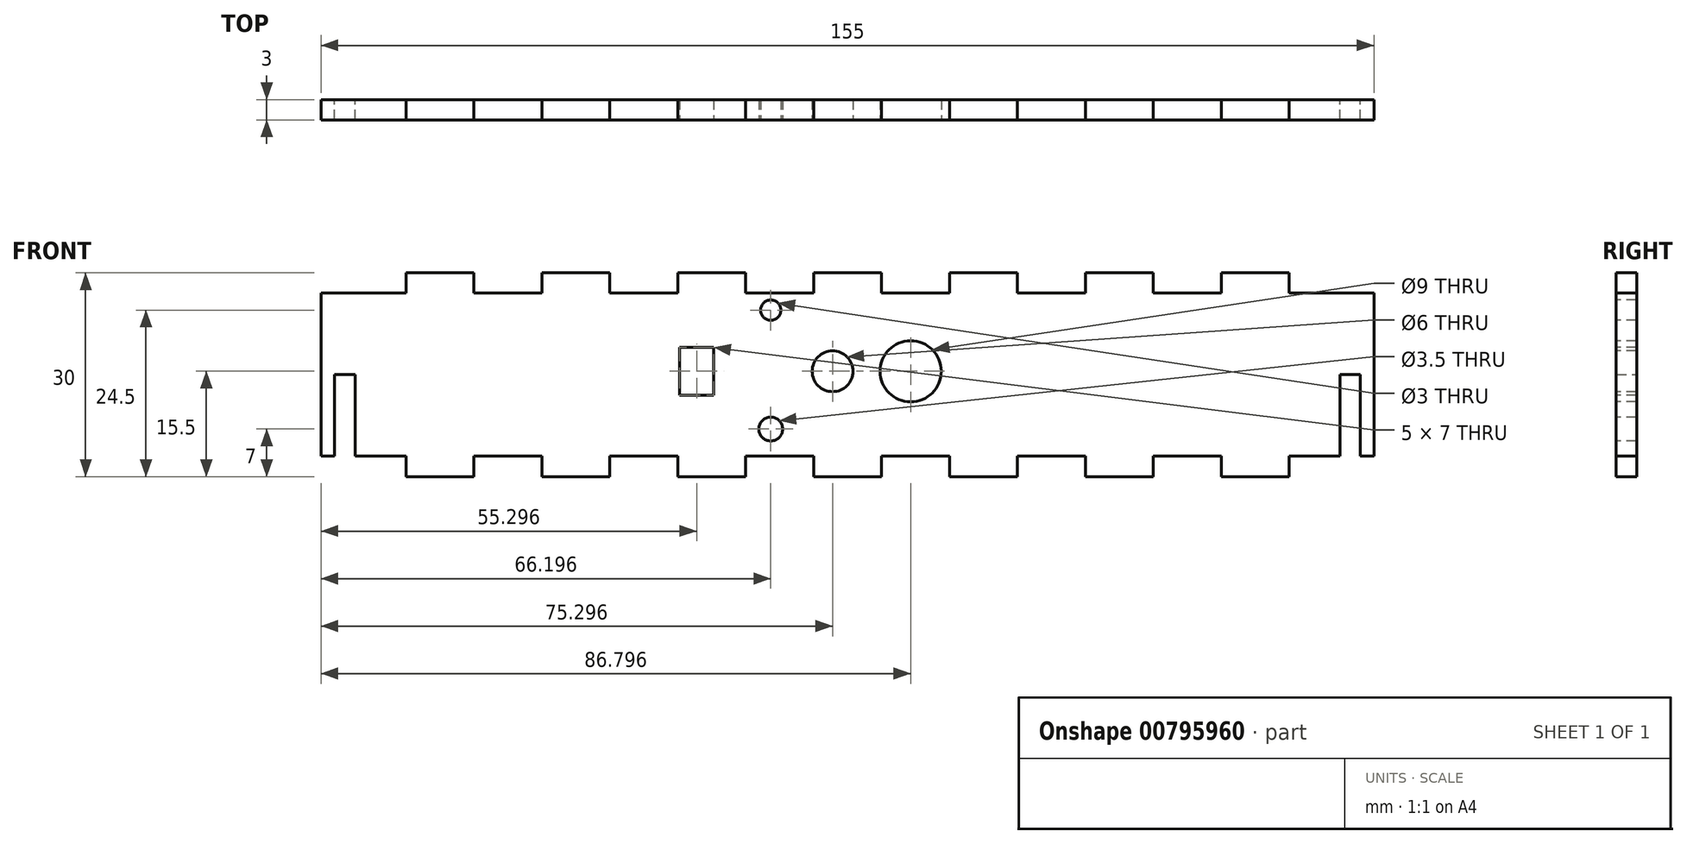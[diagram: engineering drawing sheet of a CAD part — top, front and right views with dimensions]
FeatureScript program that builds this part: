
annotation { "Feature Type Name" : "Feature", "Feature Type Description" : "" }
export const myFeature = defineFeature(function(context is Context, id is Id, definition is map)
    precondition{}
    {
        {
            var Q0;
            Q0=qCreatedBy(makeId("Front.planeOp"),FACE);
            var sketch = newSketch(context, id + "F0", { "sketchPlane" : qUnion([Q0])});
            skLineSegment(sketch, "E0.bottom", {"start": v(75.5, 15) * mm, "end": v(-75.5, 15) * mm});
            skLineSegment(sketch, "E0.top", {"start": v(75.5, -15) * mm, "end": v(-75.5, -15) * mm});
            skLineSegment(sketch, "E0.left", {"start": v(75.5, 15) * mm, "end": v(75.5, -15) * mm});
            skLineSegment(sketch, "E0.right", {"start": v(-75.5, 15) * mm, "end": v(-75.5, -15) * mm});
            skPoint(sketch, "E0.middle", {"position": v(0, 0) * mm});
            skSolve(sketch);
        }
        {
            var Q0;
            Q0=makeQuery(id+"F0.imprint","IMPRINT",FACE,{"disambiguationData":[TD([[makeQuery(id+"F0.imprint","IMPRINT",EDGE,{"derivedFrom":sQuery(id+"F0.wireOp",EDGE,"E0.bottom")}),1.0]])]});
            extrude(context, id + "F1", {"entities" : qUnion([Q0]), "depth" : 3 * mm, "offsetDistance" : 25 * mm});
        }
        {
            var Q0;
            Q0=makeQuery(id+"F1.opExtrude","CAP_FACE",FACE,{"disambiguationData":[OSD([sQuery(id+"F0.wireOp",EDGE,"E0.bottom"),sQuery(id+"F0.wireOp",EDGE,"E0.top"),sQuery(id+"F0.wireOp",EDGE,"E0.left"),sQuery(id+"F0.wireOp",EDGE,"E0.right")])],"isStart":false});
            var sketch = newSketch(context, id + "F2", { "sketchPlane" : qUnion([Q0])});
            skLineSegment(sketch, "E1.bottom", {"start": v(-75, -15) * mm, "end": v(-65, -15) * mm});
            skLineSegment(sketch, "E1.top", {"start": v(-75, -12) * mm, "end": v(-65, -12) * mm});
            skLineSegment(sketch, "E1.left", {"start": v(-75, -15) * mm, "end": v(-75, -12) * mm});
            skLineSegment(sketch, "E1.right", {"start": v(-65, -15) * mm, "end": v(-65, -12) * mm});
            skLineSegment(sketch, "E2.0.1.0", {"start": v(-75, 12) * mm, "end": v(-65, 12) * mm});
            skLineSegment(sketch, "E2.0.1.1", {"start": v(-75, 15) * mm, "end": v(-65, 15) * mm});
            skLineSegment(sketch, "E2.0.1.2", {"start": v(-75, 12) * mm, "end": v(-75, 15) * mm});
            skLineSegment(sketch, "E2.0.1.3", {"start": v(-65, 12) * mm, "end": v(-65, 15) * mm});
            skLineSegment(sketch, "E2.1.0.0", {"start": v(-55, -15) * mm, "end": v(-45, -15) * mm});
            skLineSegment(sketch, "E2.1.0.1", {"start": v(-55, -12) * mm, "end": v(-45, -12) * mm});
            skLineSegment(sketch, "E2.1.0.2", {"start": v(-55, -15) * mm, "end": v(-55, -12) * mm});
            skLineSegment(sketch, "E2.1.0.3", {"start": v(-45, -15) * mm, "end": v(-45, -12) * mm});
            skLineSegment(sketch, "E2.1.1.0", {"start": v(-55, 12) * mm, "end": v(-45, 12) * mm});
            skLineSegment(sketch, "E2.1.1.1", {"start": v(-55, 15) * mm, "end": v(-45, 15) * mm});
            skLineSegment(sketch, "E2.1.1.2", {"start": v(-55, 12) * mm, "end": v(-55, 15) * mm});
            skLineSegment(sketch, "E2.1.1.3", {"start": v(-45, 12) * mm, "end": v(-45, 15) * mm});
            skLineSegment(sketch, "E2.2.0.0", {"start": v(-35, -15) * mm, "end": v(-25, -15) * mm});
            skLineSegment(sketch, "E2.2.0.1", {"start": v(-35, -12) * mm, "end": v(-25, -12) * mm});
            skLineSegment(sketch, "E2.2.0.2", {"start": v(-35, -15) * mm, "end": v(-35, -12) * mm});
            skLineSegment(sketch, "E2.2.0.3", {"start": v(-25, -15) * mm, "end": v(-25, -12) * mm});
            skLineSegment(sketch, "E2.2.1.0", {"start": v(-35, 12) * mm, "end": v(-25, 12) * mm});
            skLineSegment(sketch, "E2.2.1.1", {"start": v(-35, 15) * mm, "end": v(-25, 15) * mm});
            skLineSegment(sketch, "E2.2.1.2", {"start": v(-35, 12) * mm, "end": v(-35, 15) * mm});
            skLineSegment(sketch, "E2.2.1.3", {"start": v(-25, 12) * mm, "end": v(-25, 15) * mm});
            skLineSegment(sketch, "E2.3.0.0", {"start": v(-15, -15) * mm, "end": v(-5, -15) * mm});
            skLineSegment(sketch, "E2.3.0.1", {"start": v(-15, -12) * mm, "end": v(-5, -12) * mm});
            skLineSegment(sketch, "E2.3.0.2", {"start": v(-15, -15) * mm, "end": v(-15, -12) * mm});
            skLineSegment(sketch, "E2.3.0.3", {"start": v(-5, -15) * mm, "end": v(-5, -12) * mm});
            skLineSegment(sketch, "E2.3.1.0", {"start": v(-15, 12) * mm, "end": v(-5, 12) * mm});
            skLineSegment(sketch, "E2.3.1.1", {"start": v(-15, 15) * mm, "end": v(-5, 15) * mm});
            skLineSegment(sketch, "E2.3.1.2", {"start": v(-15, 12) * mm, "end": v(-15, 15) * mm});
            skLineSegment(sketch, "E2.3.1.3", {"start": v(-5, 12) * mm, "end": v(-5, 15) * mm});
            skLineSegment(sketch, "E2.4.0.0", {"start": v(5, -15) * mm, "end": v(15, -15) * mm});
            skLineSegment(sketch, "E2.4.0.1", {"start": v(5, -12) * mm, "end": v(15, -12) * mm});
            skLineSegment(sketch, "E2.4.0.2", {"start": v(5, -15) * mm, "end": v(5, -12) * mm});
            skLineSegment(sketch, "E2.4.0.3", {"start": v(15, -15) * mm, "end": v(15, -12) * mm});
            skLineSegment(sketch, "E2.4.1.0", {"start": v(5, 12) * mm, "end": v(15, 12) * mm});
            skLineSegment(sketch, "E2.4.1.1", {"start": v(5, 15) * mm, "end": v(15, 15) * mm});
            skLineSegment(sketch, "E2.4.1.2", {"start": v(5, 12) * mm, "end": v(5, 15) * mm});
            skLineSegment(sketch, "E2.4.1.3", {"start": v(15, 12) * mm, "end": v(15, 15) * mm});
            skLineSegment(sketch, "E2.5.0.0", {"start": v(25, -15) * mm, "end": v(35, -15) * mm});
            skLineSegment(sketch, "E2.5.0.1", {"start": v(25, -12) * mm, "end": v(35, -12) * mm});
            skLineSegment(sketch, "E2.5.0.2", {"start": v(25, -15) * mm, "end": v(25, -12) * mm});
            skLineSegment(sketch, "E2.5.0.3", {"start": v(35, -15) * mm, "end": v(35, -12) * mm});
            skLineSegment(sketch, "E2.5.1.0", {"start": v(25, 12) * mm, "end": v(35, 12) * mm});
            skLineSegment(sketch, "E2.5.1.1", {"start": v(25, 15) * mm, "end": v(35, 15) * mm});
            skLineSegment(sketch, "E2.5.1.2", {"start": v(25, 12) * mm, "end": v(25, 15) * mm});
            skLineSegment(sketch, "E2.5.1.3", {"start": v(35, 12) * mm, "end": v(35, 15) * mm});
            skLineSegment(sketch, "E2.6.0.0", {"start": v(45, -15) * mm, "end": v(55, -15) * mm});
            skLineSegment(sketch, "E2.6.0.1", {"start": v(45, -12) * mm, "end": v(55, -12) * mm});
            skLineSegment(sketch, "E2.6.0.2", {"start": v(45, -15) * mm, "end": v(45, -12) * mm});
            skLineSegment(sketch, "E2.6.0.3", {"start": v(55, -15) * mm, "end": v(55, -12) * mm});
            skLineSegment(sketch, "E2.6.1.0", {"start": v(45, 12) * mm, "end": v(55, 12) * mm});
            skLineSegment(sketch, "E2.6.1.1", {"start": v(45, 15) * mm, "end": v(55, 15) * mm});
            skLineSegment(sketch, "E2.6.1.2", {"start": v(45, 12) * mm, "end": v(45, 15) * mm});
            skLineSegment(sketch, "E2.6.1.3", {"start": v(55, 12) * mm, "end": v(55, 15) * mm});
            skLineSegment(sketch, "E2.7.0.0", {"start": v(65, -15) * mm, "end": v(75, -15) * mm});
            skLineSegment(sketch, "E2.7.0.1", {"start": v(65, -12) * mm, "end": v(75, -12) * mm});
            skLineSegment(sketch, "E2.7.0.2", {"start": v(65, -15) * mm, "end": v(65, -12) * mm});
            skLineSegment(sketch, "E2.7.0.3", {"start": v(75, -15) * mm, "end": v(75, -12) * mm});
            skLineSegment(sketch, "E2.7.1.0", {"start": v(65, 12) * mm, "end": v(75, 12) * mm});
            skLineSegment(sketch, "E2.7.1.1", {"start": v(65, 15) * mm, "end": v(75, 15) * mm});
            skLineSegment(sketch, "E2.7.1.2", {"start": v(65, 12) * mm, "end": v(65, 15) * mm});
            skLineSegment(sketch, "E2.7.1.3", {"start": v(75, 12) * mm, "end": v(75, 15) * mm});
            skLineSegment(sketch, "E2.direction1", {"start": v(-75, -15) * mm, "end": v(-55, -15) * mm, "construction": true});
            skLineSegment(sketch, "E2.direction2", {"start": v(-75, -15) * mm, "end": v(-75, 12) * mm, "construction": true});
            skLineSegment(sketch, "E3.bottom", {"start": v(-70, 12) * mm, "end": v(-81.45, 12) * mm});
            skLineSegment(sketch, "E3.top", {"start": v(-70, 15) * mm, "end": v(-81.45, 15) * mm});
            skLineSegment(sketch, "E3.left", {"start": v(-70, 12) * mm, "end": v(-70, 15) * mm});
            skLineSegment(sketch, "E3.right", {"start": v(-81.45, 12) * mm, "end": v(-81.45, 15) * mm});
            skLineSegment(sketch, "E4.0.1.0", {"start": v(-70, -15) * mm, "end": v(-70, -12) * mm});
            skLineSegment(sketch, "E4.0.1.1", {"start": v(-81.45, -15) * mm, "end": v(-81.45, -12) * mm});
            skLineSegment(sketch, "E4.0.1.2", {"start": v(-70, -12) * mm, "end": v(-81.45, -12) * mm});
            skLineSegment(sketch, "E4.0.1.3", {"start": v(-70, -15) * mm, "end": v(-81.45, -15) * mm});
            skLineSegment(sketch, "E4.1.0.0", {"start": v(80, 12) * mm, "end": v(80, 15) * mm});
            skLineSegment(sketch, "E4.1.0.1", {"start": v(68.55, 12) * mm, "end": v(68.55, 15) * mm});
            skLineSegment(sketch, "E4.1.0.2", {"start": v(80, 15) * mm, "end": v(68.55, 15) * mm});
            skLineSegment(sketch, "E4.1.0.3", {"start": v(80, 12) * mm, "end": v(68.55, 12) * mm});
            skLineSegment(sketch, "E4.1.1.0", {"start": v(80, -15) * mm, "end": v(80, -12) * mm});
            skLineSegment(sketch, "E4.1.1.1", {"start": v(68.55, -15) * mm, "end": v(68.55, -12) * mm});
            skLineSegment(sketch, "E4.1.1.2", {"start": v(80, -12) * mm, "end": v(68.55, -12) * mm});
            skLineSegment(sketch, "E4.1.1.3", {"start": v(80, -15) * mm, "end": v(68.55, -15) * mm});
            skLineSegment(sketch, "E4.direction1", {"start": v(-81.45, 12) * mm, "end": v(68.55, 12) * mm, "construction": true});
            skLineSegment(sketch, "E4.direction2", {"start": v(-81.45, 12) * mm, "end": v(-81.45, -15) * mm, "construction": true});
            skCircle(sketch, "E5", {"center": v(9.3, 0.5) * mm, "radius": 4.5 * mm});
            skCircle(sketch, "E6", {"center": v(-11.3, 9.5) * mm, "radius": 1.5 * mm});
            skCircle(sketch, "E7", {"center": v(-11.3, -8) * mm, "radius": 1.75 * mm});
            skCircle(sketch, "E8", {"center": v(-2.2, 0.5) * mm, "radius": 3 * mm});
            skLineSegment(sketch, "E9.bottom", {"start": v(-24.7, -3) * mm, "end": v(-19.7, -3) * mm});
            skLineSegment(sketch, "E9.top", {"start": v(-24.7, 4) * mm, "end": v(-19.7, 4) * mm});
            skLineSegment(sketch, "E9.left", {"start": v(-24.7, -3) * mm, "end": v(-24.7, 4) * mm});
            skLineSegment(sketch, "E9.right", {"start": v(-19.7, -3) * mm, "end": v(-19.7, 4) * mm});
            skPoint(sketch, "E9.middle", {"position": v(-22.2, 0.5) * mm});
            skSolve(sketch);
        }
        {
            var Q0;
            Q0=qSketchRegion(id+"F2",true);
            extrude(context, id + "F3", {"entities" : qUnion([Q0]), "operationType" : NewBodyOperationType.REMOVE, "oppositeDirection" : true, "depth" : 25 * mm, "offsetDistance" : 25 * mm});
        }
        {
            var Q0;
            Q0=makeQuery(id+"F1.opExtrude","SWEPT_FACE",FACE,{"disambiguationData":[OSD([sQuery(id+"F0.wireOp",EDGE,"E0.left")])]});
            extrude(context, id + "F4", {"entities" : qUnion([Q0]), "operationType" : NewBodyOperationType.ADD, "depth" : 2 * mm, "offsetDistance" : 25 * mm});
        }
        {
            var Q0;
            Q0=makeQuery(id+"F1.opExtrude","SWEPT_FACE",FACE,{"disambiguationData":[OSD([sQuery(id+"F0.wireOp",EDGE,"E0.right")])]});
            extrude(context, id + "F5", {"entities" : qUnion([Q0]), "operationType" : NewBodyOperationType.ADD, "depth" : 2 * mm, "offsetDistance" : 25 * mm});
        }
        {
            var Q0;
            {var subQ0=sQuery(id+"F0.wireOp",EDGE,"E0.right");var subQ1=sQuery(id+"F0.wireOp",EDGE,"E0.left");Q0=makeQuery(id+"F5.boolean.opBoolean","MERGE",FACE,{"derivedFrom":[makeQuery(id+"F4.boolean.opBoolean","MERGE",FACE,{"derivedFrom":[makeQuery(id+"F1.opExtrude","CAP_FACE",FACE,{"disambiguationData":[OSD([sQuery(id+"F0.wireOp",EDGE,"E0.bottom"),sQuery(id+"F0.wireOp",EDGE,"E0.top"),subQ1,subQ0])],"isStart":true}),makeQuery(id+"F4.opExtrude","SWEPT_FACE",FACE,{"disambiguationData":[OSD([subQ1]),TDD([makeQuery(id+"F1.opExtrude","CAP_EDGE",EDGE,{"disambiguationData":[OSD([subQ1])],"isStart":true})])]})]}),makeQuery(id+"F5.opExtrude","SWEPT_FACE",FACE,{"disambiguationData":[OSD([subQ0]),TDD([makeQuery(id+"F1.opExtrude","CAP_EDGE",EDGE,{"disambiguationData":[OSD([subQ0])],"isStart":true})])]})]});}
            var sketch = newSketch(context, id + "F6", { "sketchPlane" : qUnion([Q0])});
            skLineSegment(sketch, "E10.bottom", {"start": v(-75.5, -12) * mm, "end": v(-72.5, -12) * mm});
            skLineSegment(sketch, "E10.top", {"start": v(-75.5, 0) * mm, "end": v(-72.5, 0) * mm});
            skLineSegment(sketch, "E10.left", {"start": v(-75.5, -12) * mm, "end": v(-75.5, 0) * mm});
            skLineSegment(sketch, "E10.right", {"start": v(-72.5, -12) * mm, "end": v(-72.5, 0) * mm});
            skLineSegment(sketch, "E11", {"start": v(0, -15) * mm, "end": v(0, 25.21) * mm, "construction": true});
            skLineSegment(sketch, "E12.MirrorCS", {"start": v(75.5, -12) * mm, "end": v(75.5, 0) * mm});
            skLineSegment(sketch, "E13.MirrorCS", {"start": v(75.5, 0) * mm, "end": v(72.5, 0) * mm});
            skLineSegment(sketch, "E14.MirrorCS", {"start": v(72.5, -12) * mm, "end": v(72.5, 0) * mm});
            skLineSegment(sketch, "E15.MirrorCS", {"start": v(75.5, -12) * mm, "end": v(72.5, -12) * mm});
            skSolve(sketch);
        }
        {
            var Q0;
            Q0=makeQuery(id+"F6.imprint","IMPRINT",FACE,{"disambiguationData":[TD([[makeQuery(id+"F6.imprint","IMPRINT",EDGE,{"derivedFrom":sQuery(id+"F6.wireOp",EDGE,"E12.MirrorCS")}),1.0]])]});
            var Q1;
            Q1=makeQuery(id+"F6.imprint","IMPRINT",FACE,{"disambiguationData":[TD([[makeQuery(id+"F6.imprint","IMPRINT",EDGE,{"derivedFrom":sQuery(id+"F6.wireOp",EDGE,"E10.bottom")}),-1.0]])]});
            extrude(context, id + "F7", {"entities" : qUnion([Q0, Q1]), "operationType" : NewBodyOperationType.REMOVE, "oppositeDirection" : true, "depth" : 25 * mm, "offsetDistance" : 25 * mm});
        }
    });
